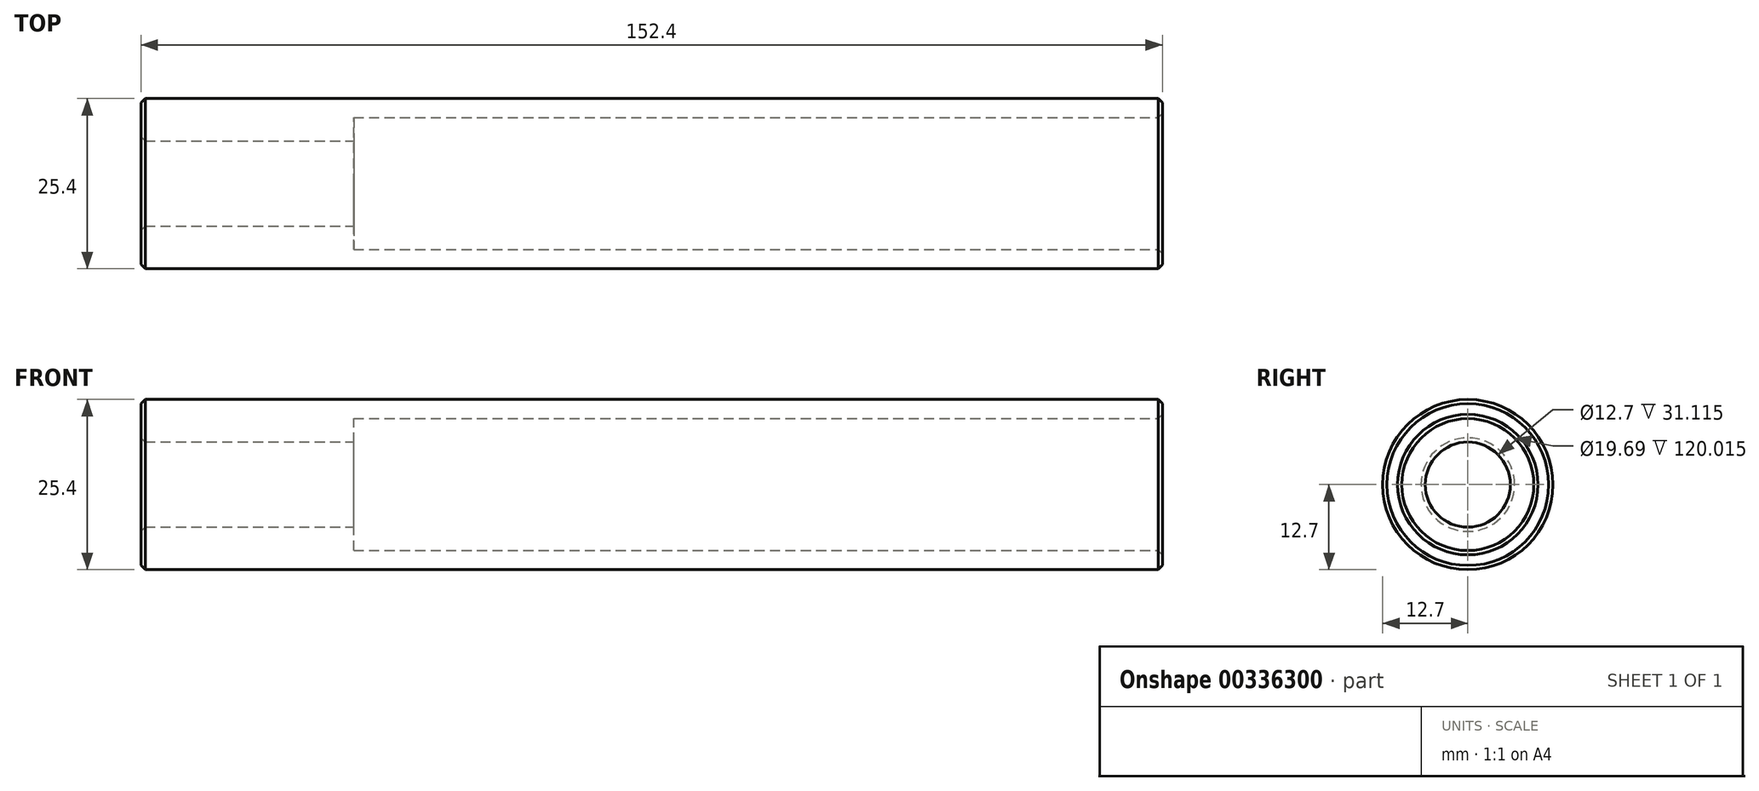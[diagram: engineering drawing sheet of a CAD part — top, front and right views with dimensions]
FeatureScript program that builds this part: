
annotation { "Feature Type Name" : "Feature", "Feature Type Description" : "" }
export const myFeature = defineFeature(function(context is Context, id is Id, definition is map)
    precondition{}
    {
        {
            var Q0;
            Q0=qCreatedBy(makeId("Front.planeOp"),FACE);
            var sketch = newSketch(context, id + "F0", { "sketchPlane" : qUnion([Q0])});
            skLineSegment(sketch, "E0", {"start": v(0, 12.7) * mm, "end": v(-152.4, 12.7) * mm});
            skLineSegment(sketch, "E1", {"start": v(-152.4, 12.7) * mm, "end": v(-152.4, 6.35) * mm});
            skLineSegment(sketch, "E2", {"start": v(-152.4, 6.35) * mm, "end": v(-120.65, 6.35) * mm});
            skLineSegment(sketch, "E3", {"start": v(-120.65, 6.35) * mm, "end": v(-120.65, 9.84) * mm});
            skLineSegment(sketch, "E4", {"start": v(-120.65, 9.84) * mm, "end": v(0, 9.84) * mm});
            skLineSegment(sketch, "E5", {"start": v(0, 9.84) * mm, "end": v(0, 12.7) * mm});
            skLineSegment(sketch, "E6", {"start": v(8.99, 0) * mm, "end": v(-183.23, 0) * mm, "construction": true});
            skSolve(sketch);
        }
        {
            var Q0;
            Q0=makeQuery(id+"F0.imprint","IMPRINT",FACE,{"disambiguationData":[TD([[makeQuery(id+"F0.imprint","IMPRINT",EDGE,{"derivedFrom":sQuery(id+"F0.wireOp",EDGE,"E0")}),1.0]])]});
            var Q1;
            Q1=sQuery(id+"F0.wireOp",EDGE,"E6");
            revolve(context, id + "F1", {"entities" : qUnion([Q0]), "axis" : qUnion([Q1]), "revolveType" : RevolveType.FULL});
        }
        {
            var Q0;
            Q0=makeQuery(id+"F1.opRevolve","SWEPT_EDGE",EDGE,{"disambiguationData":[OSD([sQuery(id+"F0.wireOp",EDGE,"E0"),sQuery(id+"F0.wireOp",EDGE,"E5")])]});
            var Q1;
            Q1=makeQuery(id+"F1.opRevolve","SWEPT_EDGE",EDGE,{"disambiguationData":[OSD([sQuery(id+"F0.wireOp",EDGE,"E4"),sQuery(id+"F0.wireOp",EDGE,"E5")])]});
            var Q2;
            Q2=makeQuery(id+"F1.opRevolve","SWEPT_EDGE",EDGE,{"disambiguationData":[OSD([sQuery(id+"F0.wireOp",EDGE,"E0"),sQuery(id+"F0.wireOp",EDGE,"E1")])]});
            var Q3;
            Q3=makeQuery(id+"F1.opRevolve","SWEPT_EDGE",EDGE,{"disambiguationData":[OSD([sQuery(id+"F0.wireOp",EDGE,"E1"),sQuery(id+"F0.wireOp",EDGE,"E2")])]});
            chamfer(context, id + "F2", {"entities" : qUnion([Q0, Q1, Q2, Q3]), "width" : 0.64 * mm, "tangentPropagation" : true});
        }
    });
